# Revit family: Plumbing-Urinals-Sloan-Valve-HYB-4000
name_source: partatom
category: Plumbing Fixtures
units: mm (PartAtom-declared; Revit-internal decimal feet)

## family parameters
Cut with Voids When Loaded = No
Host = Face
OmniClass Number = 23.45.05.21.11.21
OmniClass Title = Urinals
Part Type = Normal
Room Calculation Point = No
Round Connector Dimension = Use Diameter
Shared = No

## types (1)
- HYB-4000
    Assembly Code = D2010
    CW Connection = Yes
    CWFU = 0
    Default Elevation = 0 "
    Depth = 14 "
    Description = Vitreous China Hybrid Urinal
    Edition number = 1
    HW Connection = No
    HWFU = 0
    Height = 22.63 "
    Keynote = 15410
    Manufacturer = Sloan Valve
    Maximum Static Pressure = 80 PSI (552 kPa)
    Model = HYB-4000
    Part Number = 1004020
    Product Material = Sloan Valve - Vitreous China - White
    Product data url = https://www.bimobject.com
    Sanitary Drain Connection Diameter = 2"
    URL = www.sloanvalve.com
    Valve Pressure Drop = 0.00 psi
    Vent Connection = No
    WFU = 5
    Waste Connection = Yes
    Water Inlet Connection Diameter = 0"
    Width = 15.38 "

## geometry (parser evidence)
native form markers: Sweep x4
no freeform markers — native parametric forms only
